# Revit family: 6_天吊埋込タイプ 消音形 単相100V_3相200V
name_source: partatom
category: 機械設備
units: mm (PartAtom-declared; Revit-internal decimal feet)

## family parameters
OmniClass タイトル = Centrifugal Fans
OmniClass 番号 = 23.75.35.17.27
パーツ タイプ = 割り込み
ロード時にボイドで切り取り = いいえ
丸型コネクタ寸法 = 直径を使用
作業面ベース = いいえ
共有 = いいえ
常に垂直 = はい
部屋計算ポイント = はい

## types (18) — shared parameters
Clearance Left = 450  [stored 1.47638 ft]
IfcExportAs = IfcFanType
IfcExportType = CENTRIFUGALFORWARDCURVED
MID静圧 = 0.0 Pa
MID風量 = 0.0 m³/h
OmniClassCode = 23-33 31 19 13 15
URL = https://www.mitsubishielectric.co.jp
Uniclass2015Code = Pr_65_67_29_12
Uniclass2015Title = Centrifugal fans
Uniclass2015Version = Systems v1.9
サービススペース = はい
ファンの種類 = 多翼形
仕様書バージョン = Version1.0
企業コード = 108420
分類コード = 50052502100020
参照している仕様書等のバージョン = 公共建築工事標準仕様書（機械設備工事編）平成31年度版
周波数 = 50 Hz
呼称 = 消音ボックス付送風機
実風量 = 0.0 m³/h
本体マテリアル = 溶融亜鉛めっき鋼板
極 = 4
法定耐用年数 = 15
盤工事区分 = 電気工事
積算_科目 = 2 換気設備
製品出荷対象 = 国内
製造元 = 三菱電機株式会社
設置方法 = 天吊
説明 = ストレートシロッコファン天吊埋込タイプ（消音形）
負荷分類 = 3_ファン類
運転質量 = 0.00 kg
zero-valued in all types: Clearance Back, Clearance Bottom, Clearance Front, Clearance Right, Clearance Top

## per-type parameters (varying)
- BFS-15SUG: Depth=360  [stored 1.1811 ft]; Height=225  [stored 0.738189 ft]; M=60  [stored 0.19685 ft]; MAX静圧=39.0 Pa; MAX風量=150.0 m³/h; MIN静圧=20.0 Pa; MIN風量=110.0 m³/h; Width=273  [stored 0.895669 ft]; ダクト径=100 mm; 価格=43500 $; 天吊金具ピッチ奥行=325  [stored 1.06627 ft]; 天吊金具ピッチ幅=349  [stored 1.14501 ft]; 形名=BFS-SUG : BFS-15SUG; 極数=2; 消費電力=21 W; 番手=#1; 相=1; 製品リリース年月=2018年4月23日; 製品質量=7.00 kg; 質量=8.40 kg; 電動機出力=8 W; 電圧=100 V; 騒音レベル(dB(A))=32; 騒音レベル(dB(A))_側面=17.5; 騒音レベル(dB(A))_吐出=32; 騒音レベル(dB(A))_吸込=20.5
- BFS-30SUG: Depth=428  [stored 1.4042 ft]; Height=225  [stored 0.738189 ft]; M=70  [stored 0.229659 ft]; MAX静圧=39.0 Pa; MAX風量=300.0 m³/h; MIN静圧=18.0 Pa; MIN風量=204.0 m³/h; Width=273  [stored 0.895669 ft]; ダクト径=150 mm; 価格=60500 $; 天吊金具ピッチ奥行=393  [stored 1.28937 ft]; 天吊金具ピッチ幅=349  [stored 1.14501 ft]; 形名=BFS-SUG : BFS-30SUG; 極数=2; 消費電力=38 W; 番手=#1; 相=1; 製品リリース年月=2018年4月23日; 製品質量=7.50 kg; 質量=9.00 kg; 電動機出力=16 W; 電圧=100 V; 騒音レベル(dB(A))=40; 騒音レベル(dB(A))_側面=18.5; 騒音レベル(dB(A))_吐出=40; 騒音レベル(dB(A))_吸込=25.5
- BFS-40SUG: Depth=454  [stored 1.4895 ft]; Height=255  [stored 0.836614 ft]; M=70  [stored 0.229659 ft]; MAX静圧=59.0 Pa; MAX風量=400.0 m³/h; MIN静圧=31.0 Pa; MIN風量=289.0 m³/h; Width=305  [stored 1.00066 ft]; ダクト径=150 mm; 価格=72400 $; 天吊金具ピッチ奥行=419; 天吊金具ピッチ幅=381  [stored 1.25 ft]; 形名=BFS-SUG : BFS-40SUG; 極数=2; 消費電力=57 W; 番手=#1 1/4; 相=1; 製品リリース年月=2018年4月23日; 製品質量=9.50 kg; 質量=11.40 kg; 電動機出力=25 W; 電圧=100 V; 騒音レベル(dB(A))=43; 騒音レベル(dB(A))_側面=19.5; 騒音レベル(dB(A))_吐出=43; 騒音レベル(dB(A))_吸込=26
- BFS-50SUG: Depth=573  [stored 1.87992 ft]; Height=255  [stored 0.836614 ft]; M=85  [stored 0.278871 ft]; MAX静圧=110.0 Pa; MAX風量=500.0 m³/h; MIN静圧=80.0 Pa; MIN風量=425.0 m³/h; Width=375  [stored 1.23031 ft]; ダクト径=200 mm; 価格=10200 $; 天吊金具ピッチ奥行=538  [stored 1.76509 ft]; 天吊金具ピッチ幅=451  [stored 1.47966 ft]; 形名=BFS-SUG : BFS-50SUG; 極数=2; 消費電力=75 W; 番手=#1 1/4; 相=1; 製品リリース年月=2018年4月23日; 製品質量=13.00 kg; 質量=15.60 kg; 電動機出力=45 W; 電圧=100 V; 騒音レベル(dB(A))=48; 騒音レベル(dB(A))_側面=21.5; 騒音レベル(dB(A))_吐出=48; 騒音レベル(dB(A))_吸込=28.5
- BFS-65SUG: Depth=638  [stored 2.09318 ft]; Height=305  [stored 1.00066 ft]; M=85  [stored 0.278871 ft]; MAX静圧=118.0 Pa; MAX風量=650.0 m³/h; MIN静圧=79.0 Pa; MIN風量=534.0 m³/h; Width=423  [stored 1.3878 ft]; ダクト径=200 mm; 価格=107000 $; 天吊金具ピッチ奥行=603; 天吊金具ピッチ幅=499  [stored 1.63714 ft]; 形名=BFS-SUG : BFS-65SUG; 極数=2; 消費電力=106 W; 番手=#1 1/4; 相=1; 製品リリース年月=2018年4月23日; 製品質量=16.00 kg; 質量=19.20 kg; 電動機出力=65 W; 電圧=100 V; 騒音レベル(dB(A))=51; 騒音レベル(dB(A))_側面=23; 騒音レベル(dB(A))_吐出=51; 騒音レベル(dB(A))_吸込=28
- BFS-80SUG: Depth=638  [stored 2.09318 ft]; Height=305  [stored 1.00066 ft]; M=85  [stored 0.278871 ft]; MAX静圧=108.0 Pa; MAX風量=800.0 m³/h; MIN静圧=70.0 Pa; MIN風量=638.0 m³/h; Width=423  [stored 1.3878 ft]; ダクト径=200 mm; 価格=114000 $; 天吊金具ピッチ奥行=603; 天吊金具ピッチ幅=499  [stored 1.63714 ft]; 形名=BFS-SUG : BFS-80SUG; 極数=2; 消費電力=136 W; 番手=#1 1/4; 相=1; 製品リリース年月=2018年4月23日; 製品質量=16.50 kg; 質量=19.80 kg; 電動機出力=80 W; 電圧=100 V; 騒音レベル(dB(A))=52; 騒音レベル(dB(A))_側面=25; 騒音レベル(dB(A))_吐出=52; 騒音レベル(dB(A))_吸込=30.5
- BFS-90SUG: Depth=638  [stored 2.09318 ft]; Height=305  [stored 1.00066 ft]; M=85  [stored 0.278871 ft]; MAX静圧=137.0 Pa; MAX風量=900.0 m³/h; MIN静圧=94.0 Pa; MIN風量=745.0 m³/h; Width=443  [stored 1.45341 ft]; ダクト径=200 mm; 価格=119000 $; 天吊金具ピッチ奥行=603; 天吊金具ピッチ幅=519; 形名=BFS-SUG : BFS-90SUG; 極数=2; 消費電力=161 W; 番手=#1 1/2; 相=1; 製品リリース年月=2018年4月23日; 製品質量=18.50 kg; 質量=22.20 kg; 電動機出力=110 W; 電圧=100 V; 騒音レベル(dB(A))=55; 騒音レベル(dB(A))_側面=27; 騒音レベル(dB(A))_吐出=55; 騒音レベル(dB(A))_吸込=33
- BFS-100SUG: Depth=638  [stored 2.09318 ft]; Height=305  [stored 1.00066 ft]; M=85  [stored 0.278871 ft]; MAX静圧=157.0 Pa; MAX風量=1000.0 m³/h; MIN静圧=135.0 Pa; MIN風量=925.0 m³/h; Width=443  [stored 1.45341 ft]; ダクト径=200 mm; 価格=128000 $; 天吊金具ピッチ奥行=603; 天吊金具ピッチ幅=519; 形名=BFS-SUG : BFS-100SUG; 極数=2; 消費電力=198 W; 番手=#1 1/2; 相=1; 製品リリース年月=2018年4月23日; 製品質量=19.00 kg; 質量=22.80 kg; 電動機出力=160 W; 電圧=100 V; 騒音レベル(dB(A))=57; 騒音レベル(dB(A))_側面=28.5; 騒音レベル(dB(A))_吐出=57; 騒音レベル(dB(A))_吸込=36
- BFS-120SUG: Depth=668; Height=350  [stored 1.14829 ft]; M=85  [stored 0.278871 ft]; MAX静圧=210.0 Pa; MAX風量=1200.0 m³/h; MIN静圧=166.0 Pa; MIN風量=1065.0 m³/h; Width=455; ダクト径=250 mm; 価格=140800 $; 天吊金具ピッチ奥行=633  [stored 2.07677 ft]; 天吊金具ピッチ幅=531  [stored 1.74213 ft]; 形名=BFS-SUG : BFS-120SUG; 極数=2; 消費電力=272 W; 番手=#1 1/2; 相=1; 製品リリース年月=2018年4月23日; 製品質量=22.00 kg; 質量=26.40 kg; 電動機出力=200 W; 電圧=100 V; 騒音レベル(dB(A))=58; 騒音レベル(dB(A))_側面=31; 騒音レベル(dB(A))_吐出=58; 騒音レベル(dB(A))_吸込=40
- BFS-150SUG: Depth=768; Height=350  [stored 1.14829 ft]; M=85  [stored 0.278871 ft]; MAX静圧=200.0 Pa; MAX風量=1500.0 m³/h; MIN静圧=150.0 Pa; MIN風量=1300.0 m³/h; Width=455; ダクト径=250 mm; 価格=146300 $; 天吊金具ピッチ奥行=733; 天吊金具ピッチ幅=531  [stored 1.74213 ft]; 形名=BFS-SUG : BFS-150SUG; 極数=2; 消費電力=368 W; 番手=#1 1/2; 相=1; 製品リリース年月=2018年4月23日; 製品質量=24.00 kg; 質量=28.80 kg; 電動機出力=340 W; 電圧=100 V; 騒音レベル(dB(A))=61.5; 騒音レベル(dB(A))_側面=32.5; 騒音レベル(dB(A))_吐出=61.5; 騒音レベル(dB(A))_吸込=41.5
- BFS-80TUG: Depth=638  [stored 2.09318 ft]; Height=305  [stored 1.00066 ft]; M=85  [stored 0.278871 ft]; MAX静圧=108.0 Pa; MAX風量=800.0 m³/h; MIN静圧=61.0 Pa; MIN風量=601.0 m³/h; Width=423  [stored 1.3878 ft]; ダクト径=200 mm; 価格=114000 $; 天吊金具ピッチ奥行=603; 天吊金具ピッチ幅=499  [stored 1.63714 ft]; 形名=BFS-TUG : BFS-80TUG; 極数=3; 消費電力=122 W; 番手=#1 1/4; 相=3; 製品リリース年月=2018年4月23日; 製品質量=18.00 kg; 質量=21.60 kg; 電動機出力=80 W; 電圧=200 V; 騒音レベル(dB(A))=52; 騒音レベル(dB(A))_側面=25; 騒音レベル(dB(A))_吐出=52; 騒音レベル(dB(A))_吸込=31.5
- BFS-90TUG: Depth=638  [stored 2.09318 ft]; Height=305  [stored 1.00066 ft]; M=85  [stored 0.278871 ft]; MAX静圧=137.0 Pa; MAX風量=900.0 m³/h; MIN静圧=80.0 Pa; MIN風量=688.0 m³/h; Width=443  [stored 1.45341 ft]; ダクト径=200 mm; 価格=119000 $; 天吊金具ピッチ奥行=603; 天吊金具ピッチ幅=519; 形名=BFS-TUG : BFS-90TUG; 極数=3; 消費電力=152 W; 番手=#1 1/2; 相=3; 製品リリース年月=2018年4月23日; 製品質量=18.00 kg; 質量=21.60 kg; 電動機出力=100 W; 電圧=200 V; 騒音レベル(dB(A))=55; 騒音レベル(dB(A))_側面=27.5; 騒音レベル(dB(A))_吐出=55; 騒音レベル(dB(A))_吸込=33.5
- BFS-100TUG: Depth=638  [stored 2.09318 ft]; Height=305  [stored 1.00066 ft]; M=85  [stored 0.278871 ft]; MAX静圧=157.0 Pa; MAX風量=1000.0 m³/h; MIN静圧=103.0 Pa; MIN風量=810.0 m³/h; Width=443  [stored 1.45341 ft]; ダクト径=200 mm; 価格=128000 $; 天吊金具ピッチ奥行=603; 天吊金具ピッチ幅=519; 形名=BFS-TUG : BFS-100TUG; 極数=3; 消費電力=181 W; 番手=#1 1/2; 相=3; 製品リリース年月=2018年4月23日; 製品質量=18.50 kg; 質量=22.20 kg; 電動機出力=150 W; 電圧=200 V; 騒音レベル(dB(A))=57; 騒音レベル(dB(A))_側面=28.5; 騒音レベル(dB(A))_吐出=57; 騒音レベル(dB(A))_吸込=36
- BFS-120TUG: Depth=668; Height=350  [stored 1.14829 ft]; M=85  [stored 0.278871 ft]; MAX静圧=210.0 Pa; MAX風量=1200.0 m³/h; MIN静圧=119.0 Pa; MIN風量=895.0 m³/h; Width=455; ダクト径=250 mm; 価格=140800 $; 天吊金具ピッチ奥行=633  [stored 2.07677 ft]; 天吊金具ピッチ幅=531  [stored 1.74213 ft]; 形名=BFS-TUG : BFS-120TUG; 極数=3; 消費電力=255 W; 番手=#1 1/2; 相=3; 製品リリース年月=2018年4月23日; 製品質量=22.00 kg; 質量=26.40 kg; 電動機出力=180 W; 電圧=200 V; 騒音レベル(dB(A))=58; 騒音レベル(dB(A))_側面=31; 騒音レベル(dB(A))_吐出=58; 騒音レベル(dB(A))_吸込=40
- BFS-150TUG: Depth=768; Height=350  [stored 1.14829 ft]; M=85  [stored 0.278871 ft]; MAX静圧=200.0 Pa; MAX風量=1500.0 m³/h; MIN静圧=120.0 Pa; MIN風量=1165.0 m³/h; Width=455; ダクト径=250 mm; 価格=146300 $; 天吊金具ピッチ奥行=733; 天吊金具ピッチ幅=531  [stored 1.74213 ft]; 形名=BFS-TUG : BFS-150TUG; 極数=3; 消費電力=372 W; 番手=#1 1/2; 相=3; 製品リリース年月=2018年4月23日; 製品質量=24.00 kg; 質量=28.80 kg; 電動機出力=280 W; 電圧=200 V; 騒音レベル(dB(A))=61.5; 騒音レベル(dB(A))_側面=32.5; 騒音レベル(dB(A))_吐出=61.5; 騒音レベル(dB(A))_吸込=41.5
- BFS-180TUG: Depth=768; Height=350  [stored 1.14829 ft]; M=85  [stored 0.278871 ft]; MAX静圧=190.0 Pa; MAX風量=1800.0 m³/h; MIN静圧=0.0 Pa; MIN風量=0.0 m³/h; Width=505  [stored 1.65682 ft]; ダクト径=250 mm; 価格=171600 $; 天吊金具ピッチ奥行=733; 天吊金具ピッチ幅=581  [stored 1.90617 ft]; 形名=BFS-TUG : BFS-180TUG; 極数=3; 消費電力=425 W; 番手=#1 1/2; 相=3; 製品リリース年月=2018年4月23日; 製品質量=26.00 kg; 質量=31.20 kg; 電動機出力=350 W; 電圧=200 V; 騒音レベル(dB(A))=63.5; 騒音レベル(dB(A))_側面=33; 騒音レベル(dB(A))_吐出=63.5; 騒音レベル(dB(A))_吸込=42.5
- BFS-210TUG: Depth=878; Height=350  [stored 1.14829 ft]; M=100  [stored 0.328084 ft]; MAX静圧=191.0 Pa; MAX風量=2100.0 m³/h; MIN静圧=0.0 Pa; MIN風量=0.0 m³/h; Width=551  [stored 1.80774 ft]; ダクト径=300 mm; 価格=225500 $; 天吊金具ピッチ奥行=843; 天吊金具ピッチ幅=627  [stored 2.05709 ft]; 形名=BFS-TUG : BFS-210TUG; 極数=3; 消費電力=540 W; 番手=#1 1/2; 相=3; 製品リリース年月=2018年4月23日; 製品質量=29.00 kg; 質量=34.80 kg; 電動機出力=490 W; 電圧=200 V; 騒音レベル(dB(A))=66; 騒音レベル(dB(A))_側面=33.5; 騒音レベル(dB(A))_吐出=66; 騒音レベル(dB(A))_吸込=44.5
- BFS-240TUA: Depth=917; Height=373  [stored 1.22375 ft]; M=99  [stored 0.324803 ft]; MAX静圧=180.0 Pa; MAX風量=2400.0 m³/h; MIN静圧=0.0 Pa; MIN風量=0.0 m³/h; Width=493  [stored 1.61745 ft]; ダクト径=300 mm; 価格=221000 $; 天吊金具ピッチ奥行=864; 天吊金具ピッチ幅=602  [stored 1.97507 ft]; 形名=BFS-TUG : BFS-240TUA; 極数=3; 消費電力=600 W; 番手=#1 1/2; 相=3; 製品リリース年月=2003年4月; 製品質量=37.00 kg; 質量=44.40 kg; 電動機出力=1100 W; 電圧=200 V; 騒音レベル(dB(A))=69; 騒音レベル(dB(A))_側面=42; 騒音レベル(dB(A))_吐出=69; 騒音レベル(dB(A))_吸込=47

note: column(s) folded — value = type name in every type: モデル

note: [stored X ft] marks values corroborated as IEEE doubles in the binary element streams (Revit-internal decimal feet)
